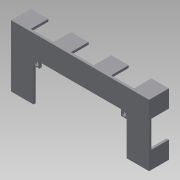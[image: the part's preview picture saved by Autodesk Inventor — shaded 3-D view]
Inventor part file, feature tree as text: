
AUTODESK INVENTOR PART (.ipt)
format: ipt  version: 2015 SP1 (Build 190203100, 203)  size: 152,064 bytes
history: native  units: mm
features: extrude x3, sketch x3, projected_geometry x1
ambient origin geometry x8: Origin, YZ Plane, XZ Plane, XY Plane, X Axis, Y Axis, Z Axis, Center Point
bodies: Solid1 (feature_tree)
feature tree (7):
  extrude  "Extrusion1"  Depth=15.0mm
  extrude  "Extrusion2"  Depth=88.597889mm
  extrude  "Extrusion3"  Depth=15.0mm
  sketch  "Sketch1"  dims[d0=3.0mm d1=0.0mm d3=15.0mm]
  sketch  "Sketch3"  dims[d4=2.0mm d5=88.597889mm]
  sketch  "Sketch5"  dims[d6=19.532667mm d7=15.0mm d8=19.532667mm d9=15.0mm d10=2.0mm d11=15.0mm d12=2.0mm d13=15.0mm d14=0.0mm d15=2.0mm d16=2.0mm d17=1.0mm d18=0.0mm]
  projected_geometry  "Projected Loop2"
